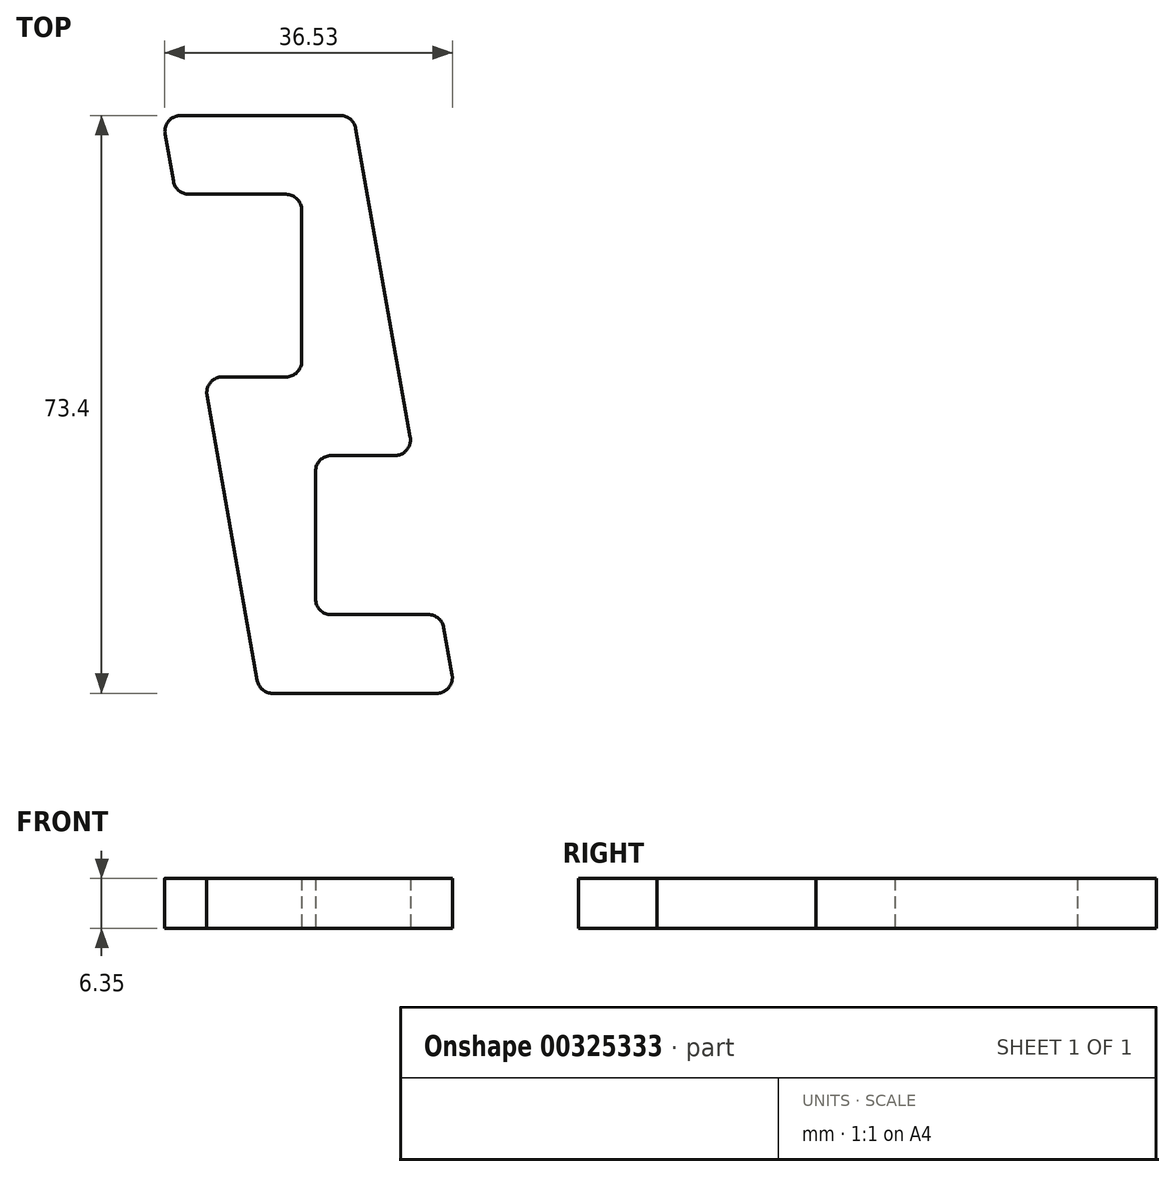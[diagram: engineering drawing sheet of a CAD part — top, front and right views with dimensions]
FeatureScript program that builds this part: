
annotation { "Feature Type Name" : "Feature", "Feature Type Description" : "" }
export const myFeature = defineFeature(function(context is Context, id is Id, definition is map)
    precondition{}
    {
        {
            var Q0;
            Q0=qCreatedBy(makeId("Top.planeOp"),FACE);
            var sketch = newSketch(context, id + "F0", { "sketchPlane" : qUnion([Q0])});
            skLineSegment(sketch, "E0", {"start": v(0, 0) * mm, "end": v(-24.88, 0) * mm});
            skLineSegment(sketch, "E1", {"start": v(-24.88, 0) * mm, "end": v(-31.96, 40.2) * mm});
            skLineSegment(sketch, "E2", {"start": v(-31.96, 40.2) * mm, "end": v(-19.53, 40.2) * mm});
            skLineSegment(sketch, "E3", {"start": v(-19.53, 40.2) * mm, "end": v(-19.53, 63.4) * mm});
            skLineSegment(sketch, "E4", {"start": v(-19.53, 63.4) * mm, "end": v(-35.53, 63.4) * mm});
            skLineSegment(sketch, "E5", {"start": v(-35.53, 63.4) * mm, "end": v(-37.29, 73.4) * mm});
            skLineSegment(sketch, "E6", {"start": v(-37.29, 73.4) * mm, "end": v(-12.94, 73.4) * mm});
            skLineSegment(sketch, "E7", {"start": v(-12.94, 73.4) * mm, "end": v(-5.33, 30.2) * mm});
            skLineSegment(sketch, "E8", {"start": v(-5.33, 30.2) * mm, "end": v(-17.76, 30.2) * mm});
            skLineSegment(sketch, "E9", {"start": v(-17.76, 30.2) * mm, "end": v(-17.76, 10) * mm});
            skLineSegment(sketch, "E10", {"start": v(-17.76, 10) * mm, "end": v(-1.76, 10) * mm});
            skLineSegment(sketch, "E11", {"start": v(-1.76, 10) * mm, "end": v(0, 0) * mm});
            skLineSegment(sketch, "E12", {"start": v(-17.76, 30.2) * mm, "end": v(-19.53, 40.2) * mm, "construction": true});
            skLineSegment(sketch, "E13", {"start": v(-19.53, 63.4) * mm, "end": v(-19.53, 73.4) * mm, "construction": true});
            skLineSegment(sketch, "E14", {"start": v(-17.76, 10) * mm, "end": v(-17.76, 0) * mm, "construction": true});
            skSolve(sketch);
        }
        {
            var Q0;
            Q0=makeQuery(id+"F0.imprint","IMPRINT",FACE,{"disambiguationData":[TD([[makeQuery(id+"F0.imprint","IMPRINT",EDGE,{"derivedFrom":sQuery(id+"F0.wireOp",EDGE,"E0")}),-1.0]])]});
            extrude(context, id + "F1", {"entities" : qUnion([Q0]), "depth" : 6.35 * mm});
        }
        {
            var Q0;
            Q0=makeQuery(id+"F1.opExtrude","SWEPT_EDGE",EDGE,{"disambiguationData":[OSD([sQuery(id+"F0.wireOp",EDGE,"E5"),sQuery(id+"F0.wireOp",EDGE,"E6")])]});
            var Q1;
            Q1=makeQuery(id+"F1.opExtrude","SWEPT_EDGE",EDGE,{"disambiguationData":[OSD([sQuery(id+"F0.wireOp",EDGE,"E4"),sQuery(id+"F0.wireOp",EDGE,"E5")])]});
            var Q2;
            Q2=makeQuery(id+"F1.opExtrude","SWEPT_EDGE",EDGE,{"disambiguationData":[OSD([sQuery(id+"F0.wireOp",EDGE,"E3"),sQuery(id+"F0.wireOp",EDGE,"E4")])]});
            var Q3;
            Q3=makeQuery(id+"F1.opExtrude","SWEPT_EDGE",EDGE,{"disambiguationData":[OSD([sQuery(id+"F0.wireOp",EDGE,"E1"),sQuery(id+"F0.wireOp",EDGE,"E2")])]});
            var Q4;
            Q4=makeQuery(id+"F1.opExtrude","SWEPT_EDGE",EDGE,{"disambiguationData":[OSD([sQuery(id+"F0.wireOp",EDGE,"E2"),sQuery(id+"F0.wireOp",EDGE,"E3")])]});
            var Q5;
            Q5=makeQuery(id+"F1.opExtrude","SWEPT_EDGE",EDGE,{"disambiguationData":[OSD([sQuery(id+"F0.wireOp",EDGE,"E6"),sQuery(id+"F0.wireOp",EDGE,"E7")])]});
            var Q6;
            Q6=makeQuery(id+"F1.opExtrude","SWEPT_EDGE",EDGE,{"disambiguationData":[OSD([sQuery(id+"F0.wireOp",EDGE,"E7"),sQuery(id+"F0.wireOp",EDGE,"E8")])]});
            var Q7;
            Q7=makeQuery(id+"F1.opExtrude","SWEPT_EDGE",EDGE,{"disambiguationData":[OSD([sQuery(id+"F0.wireOp",EDGE,"E8"),sQuery(id+"F0.wireOp",EDGE,"E9")])]});
            var Q8;
            Q8=makeQuery(id+"F1.opExtrude","SWEPT_EDGE",EDGE,{"disambiguationData":[OSD([sQuery(id+"F0.wireOp",EDGE,"E9"),sQuery(id+"F0.wireOp",EDGE,"E10")])]});
            var Q9;
            Q9=makeQuery(id+"F1.opExtrude","SWEPT_EDGE",EDGE,{"disambiguationData":[OSD([sQuery(id+"F0.wireOp",EDGE,"E10"),sQuery(id+"F0.wireOp",EDGE,"E11")])]});
            var Q10;
            Q10=makeQuery(id+"F1.opExtrude","SWEPT_EDGE",EDGE,{"disambiguationData":[OSD([sQuery(id+"F0.wireOp",EDGE,"E0"),sQuery(id+"F0.wireOp",EDGE,"E11")])]});
            var Q11;
            Q11=makeQuery(id+"F1.opExtrude","SWEPT_EDGE",EDGE,{"disambiguationData":[OSD([sQuery(id+"F0.wireOp",EDGE,"E0"),sQuery(id+"F0.wireOp",EDGE,"E1")])]});
            fillet(context, id + "F2", {"entities" : qUnion([Q0, Q1, Q2, Q3, Q4, Q5, Q6, Q7, Q8, Q9, Q10, Q11]), "radius" : 2 * mm, "tangentPropagation" : true, "allowEdgeOverflow" : false});
        }
    });
